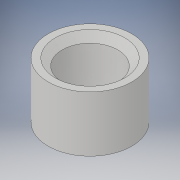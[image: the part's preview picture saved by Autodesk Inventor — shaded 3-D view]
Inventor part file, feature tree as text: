
AUTODESK INVENTOR PART (.ipt)
format: ipt  version: 2018 (Build 220112000, 112)  size: 101,888 bytes
history: native  units: in
note: dims shown in document units (in); Inventor stores cm internally (conversion verified against a paired STEP export)
features: extrude x1, chamfer x1, sketch x1
ambient origin geometry x8: Origin, YZ Plane, XZ Plane, XY Plane, X Axis, Y Axis, Z Axis, Center Point
bodies: Solid1 (feature_tree)
feature tree (3):
  extrude  "Extrusion1"  Depth=1.0in
  chamfer  "Chamfer1"  Distance=1.0in
  sketch  "Sketch3"  dims[d7=1.0in d8=1.5in d9=1.0in d10=0.0in d11=0.125in d12=0.125in d13=45.0deg]
